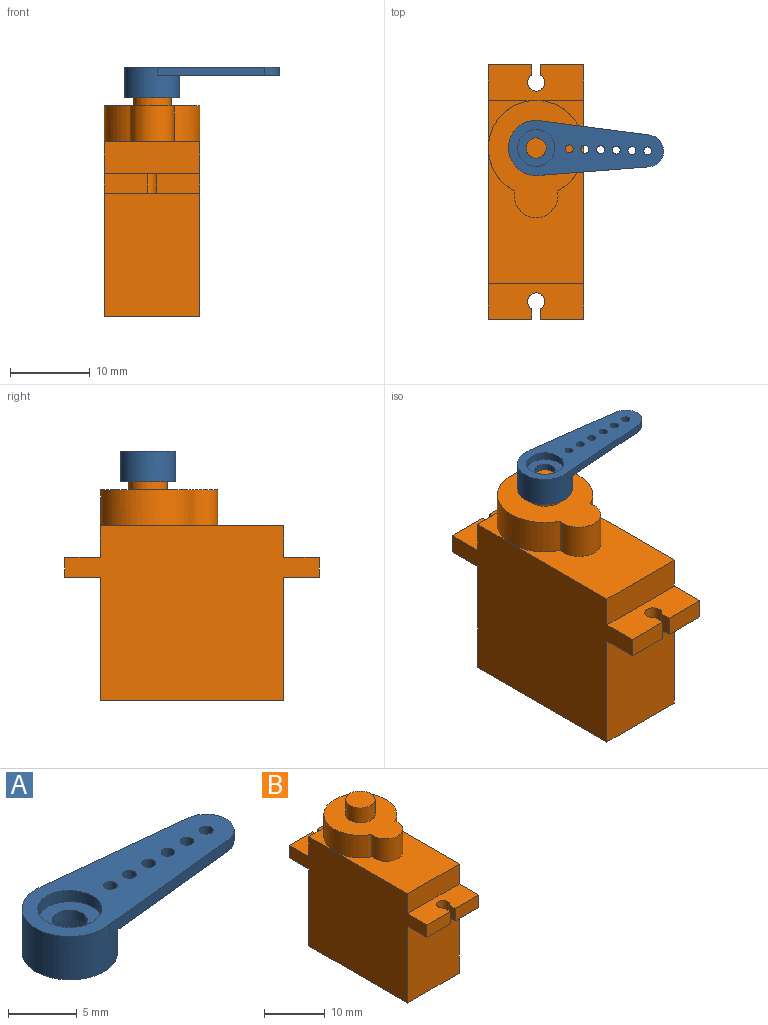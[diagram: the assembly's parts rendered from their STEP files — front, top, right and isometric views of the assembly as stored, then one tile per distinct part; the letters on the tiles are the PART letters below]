
ASSEMBLY  parts=2 mates=1
PART A: 18 faces, bbox 19.5x7x3.9 mm
  f0: cylinder r=3.47mm len=6.95mm, axis (0,0,-1), area 74.6mm2, adj f1,f2,f5,f6,f8
  f1: plane 19.5x6.95mm, normal (0,0,1), area 80.7mm2, adj f0,f5,f6,f7,f9,f12,f13,f14
  f2: plane 6.95x6.95mm, normal (0,0,-1), area 19.5mm2, adj f0,f3
  f3: cylinder r=2.43mm len=4.85mm, axis (0,0,-1), area 30.5mm2, adj f2,f4
  f4: plane 4.85x4.85mm, normal (0,0,-1), area 13.4mm2, adj f3,f11
  f5: plane 13.51x1.4mm, normal (0.1,0.99,0), area 13.6mm2, adj f0,f1,f7,f8
  f6: plane 13.51x1.4mm, normal (0.1,-0.99,0), area 13.6mm2, adj f0,f1,f7,f8
  f7: cylinder r=2.01mm len=4mm, axis (0,0,1), area 5.9mm2, adj f1,f5,f6,f8
  f8: plane 15.31x6.8mm, normal (0,0,-1), area 59.7mm2, adj f0,f5,f6,f7,f12,f13,f14,f15
  f9: cylinder r=2.32mm len=4.65mm, axis (0,0,1), area 14.6mm2, adj f1,f10
  f10: plane 4.65x4.65mm, normal (0,0,1), area 11.9mm2, adj f9,f11
  f11: cylinder r=1.28mm len=2.55mm, axis (0,0,1), area 6.8mm2, adj f4,f10
  f12: cylinder r=0.5mm len=1mm, axis (0,0,1), area 3.1mm2, adj f1,f8
  f13: cylinder r=0.5mm len=1mm, axis (0,0,1), area 3.1mm2, adj f1,f8
  f14: cylinder r=0.5mm len=1mm, axis (0,0,1), area 3.1mm2, adj f1,f8
  f15: cylinder r=0.5mm len=1mm, axis (0,0,1), area 3.1mm2, adj f1,f8
  f16: cylinder r=0.5mm len=1mm, axis (0,0,1), area 3.1mm2, adj f1,f8
  f17: cylinder r=0.5mm len=1mm, axis (0,0,1), area 3.1mm2, adj f1,f8
PART B: 29 faces, bbox 12x32x29.5 mm
  f0: plane 17x12mm, normal (0,0,1), area 134.4mm2, adj f9,f10,f11,f24,f25
  f1: plane 6x6mm, normal (0,0,1), area 7.7mm2, adj f8,f11,f25
  f2: plane 5.43x2.5mm, normal (0,1,0), area 13.6mm2, adj f4,f5,f11,f22
  f3: plane 5.43x2.5mm, normal (0,-1,0), area 13.6mm2, adj f11,f16,f17,f19
  f4: plane 12x4.5mm, normal (0,0,1), area 49mm2, adj f2,f8,f9,f11,f14,f21,f22,f23
  f5: plane 12x4.5mm, normal (0,0,-1), area 49mm2, adj f2,f7,f9,f11,f14,f21,f22,f23
  f6: plane 15.5x12mm, normal (0,-1,0), area 186mm2, adj f9,f11,f13,f17
  f7: plane 15.5x12mm, normal (0,1,0), area 186mm2, adj f5,f9,f11,f13
  f8: plane 12x4mm, normal (0,1,0), area 48mm2, adj f1,f4,f9,f11,f12
  f9: plane 32x22mm, normal (-1,0,0), area 528.5mm2, adj f0,f4,f5,f6,f7,f8,f10,f12
  f10: plane 12x4mm, normal (0,-1,0), area 48mm2, adj f0,f9,f11,f16
  f11: plane 32x22mm, normal (1,0,0), area 528.5mm2, adj f0,f1,f2,f3,f4,f5,f6,f7
  f12: plane 6x6mm, normal (0,0,1), area 7.7mm2, adj f8,f9,f25
  f13: plane 23x12mm, normal (0,0,-1), area 276mm2, adj f6,f7,f9,f11
  f14: plane 5.43x2.5mm, normal (0,1,0), area 13.6mm2, adj f4,f5,f9,f23
  f15: plane 5.43x2.5mm, normal (0,-1,0), area 13.6mm2, adj f9,f16,f17,f18
  f16: plane 12x4.5mm, normal (0,0,1), area 49mm2, adj f3,f9,f10,f11,f15,f18,f19,f20
  f17: plane 12x4.5mm, normal (0,0,-1), area 49mm2, adj f3,f6,f9,f11,f15,f18,f19,f20
  f18: plane 2.5x1.34mm, normal (1,0,0), area 3.4mm2, adj f15,f16,f17,f20
  f19: plane 2.5x1.34mm, normal (-1,0,0), area 3.4mm2, adj f3,f16,f17,f20
  f20: cylinder r=1.07mm len=2.5mm, axis (0,0,1), area 13.9mm2, adj f16,f17,f18,f19
  f21: cylinder r=1.07mm len=2.5mm, axis (0,0,1), area 13.9mm2, adj f4,f5,f22,f23
  f22: plane 2.5x1.34mm, normal (-1,0,0), area 3.4mm2, adj f2,f4,f5,f21
  f23: plane 2.5x1.34mm, normal (1,0,0), area 3.4mm2, adj f4,f5,f14,f21
  f24: cylinder r=2.75mm len=5.5mm, axis (0,0,-1), area 44.6mm2, adj f0,f25,f26
  f25: cylinder r=6mm len=12mm, axis (0,0,-1), area 144.7mm2, adj f0,f1,f12,f24,f26
  f26: plane 14.75x12mm, normal (0,0,1), area 107.7mm2, adj f24,f25,f27
  f27: cylinder r=2.43mm len=4.85mm, axis (0,0,-1), area 45.7mm2, adj f26,f28
  f28: plane 4.85x4.85mm, normal (0,0,1), area 18.5mm2, adj f27
PLACE A rot(axis=(0,0,-1),1.5deg) t=(0,5.5,27.5)mm
PLACE B t=(-6,-11.5,0)mm
MATE revolute A.f0 <-> B.f25  axis (0,0,-1) through (0,5.5,29.5)mm
